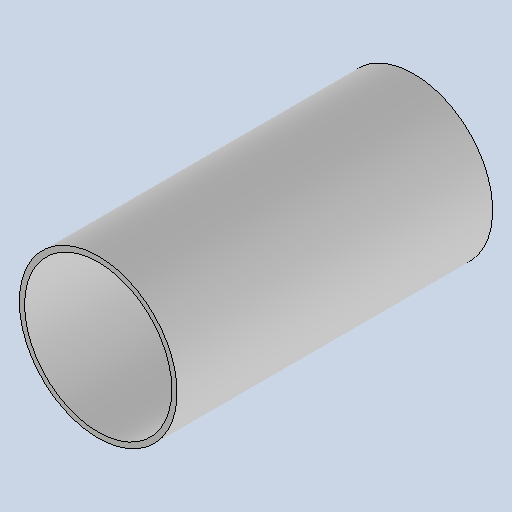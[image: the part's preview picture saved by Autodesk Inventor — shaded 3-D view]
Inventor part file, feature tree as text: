
AUTODESK INVENTOR PART (.ipt)
format: ipt  version: 2025.1 (Build 291241020, 241B)  size: 102,912 bytes
history: native  units: mm
features: extrude x1, sketch x1
ambient origin geometry x8: Origin, YZ Plane, XZ Plane, XY Plane, X Axis, Y Axis, Z Axis, Center Point
bodies: Solid1 (feature_tree)
feature tree (2):
  extrude  "Extrusion1"  Depth=180.0mm
  sketch  "Sketch1"  dims[d0=90.0mm d1=3.0mm d2=180.0mm d3=0.0mm]
